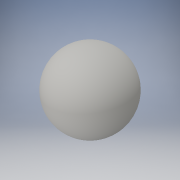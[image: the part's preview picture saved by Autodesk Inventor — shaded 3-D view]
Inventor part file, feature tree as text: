
AUTODESK INVENTOR PART (.ipt)
format: ipt  version: 2016 (Build 200138000, 138)  size: 157,184 bytes
history: native  units: in
note: dims shown in document units (in); Inventor stores cm internally (conversion verified against a paired STEP export)
features: revolve x1, sketch x1
ambient origin geometry x8: Origin, YZ Plane, XZ Plane, XY Plane, X Axis, Y Axis, Z Axis, Center Point
bodies: Solid1 (feature_tree)
feature tree (2):
  revolve  "Revolution1"  [1 undecoded]
  sketch  "Sketch1"  dims[d0=0.6in d1=0.0037in d2=90.0deg]
note: 1 required parameter value undecoded (feature->parameter linkage not recoverable at this tier; creation-order binding heuristic only, values carry confidence <= 0.55)
